# Revit family: Evoflat MSS_Circulation_RFA_1
name_source: partatom
category: Mechanical Equipment
units: mm (PartAtom-declared; Revit-internal decimal feet)

## family parameters
Always vertical = Yes
Classification = None
Cut with Voids When Loaded = No
OmniClass Number = 23.75.65.11.11
OmniClass Title = Heating Controllers
Part Type = Normal
Room Calculation Point = No
Round Connector Dimension = Use Diameter
Shared = No
Work Plane-Based = No

## types (9) — shared parameters
Circulation Pump = Yes
Connection = G 3/4 Internal Thread
D = 20 mm  [stored 0.0656168 ft]
Description = Flat Station
H1 = 5 mm  [stored 0.0164042 ft]
H2 = 13 mm
H3 = 575 mm  [stored 1.88648 ft]
H4 = 313 mm
Heating Capacity = 15 kW
Heating Circuit dT = 20 °C
Heating Flow Rate Supply = 645 l/h
Heating Total Pressure Loss Primary = 8 kPa
IfcExportAs = IfcFlowController
IfcExportType = EvoFlat MSS
Insulation Material = Danfoss EPP insulation
L = 545 mm  [stored 1.78806 ft]
L1 = 112 mm  [stored 0.367454 ft]
L1a = 43 mm  [stored 0.141076 ft]
LOD 200 = No
LOD 350 = Yes
Manufacturer = Danfoss
Max Supply Temperature = 95 °C
Nominal Pressure = PN 10
Nut size = 30 mm
Type Image = <None>
Voltage = 230 V
W = 150 mm
W1 = 44 mm  [stored 0.144357 ft]
Weight = 10.00 kg

## per-type parameters (varying)
| type | DHW Flow Rate Primary | DHW Pressure Loss Primary | DHW Tap Load 50°C | DHW Temperature DHS/DHR | DHW capacity | Front Insulation | HEX material | Model | Model Type | With Front Insulation |
| Evoflat MSS_Type 1_Cu_Circulation_145B1900 | 850 l/h | 40 kPa | 15.3 l/min | 65/22 °C | 43 kW | No | Danfoss Copper | 145B1900 | Evoflat MSS_Type 1_Cu_Circulation | No |
| Evoflat MSS_Type 2_Cu_Circulation_145B1903 | 950 l/h | 30 kPa | 17.5 l/min | 65/21 °C | 49 kW | No | Danfoss Copper | 145B1903 | Evoflat MSS_Type 2_Cu_Circulation | No |
| Evoflat MSS_Type 3_Cu_Circulation_145B1907 | 950 l/h | 27 kPa | 19.4 l/min | 65/16 °C | 55 kW | No | Danfoss Copper | 145B1907 | Evoflat MSS_Type 3_Cu_Circulation | No |
| Evoflat MSS_Type 1_Cu_Ins_Circulation_145B1910 | 850 l/h | 40 kPa | 15.3 l/min | 65/22 °C | 43 kW | Yes | Danfoss Copper | 145B1910 | Evoflat MSS_Type 1_Cu_Ins_Circulation | Yes |
| Evoflat MSS_Type 2_Cu_Ins_Circulation_145B1913 | 950 l/h | 30 kPa | 17.5 l/min | 65/21 °C | 49 kW | Yes | Danfoss Copper | 145B1913 | Evoflat MSS_Type 2_Cu_Ins_Circulation | Yes |
| Evoflat MSS_Type 3_Cu_Ins_Circulation_145B1917 | 950 l/h | 27 kPa | 19.4 l/min | 65/16 °C | 55 kW | Yes | Danfoss Copper | 145B1917 | Evoflat MSS_Type 3_Cu_Ins_Circulation | Yes |
| Evoflat MSS_Type 1_StS_Ins_Circulation_145B1954 | 850 l/h | 40 kPa | 15.3 l/min | 65/22 °C | 43 kW | Yes | Danfoss Stainless Steel | 145B1954 | Evoflat MSS_Type 1_StS_Ins_Circulation | Yes |
| Evoflat MSS_Type 2_StS_Ins_Circulation_145B1955 | 950 l/h | 30 kPa | 17.5 l/min | 65/21 °C | 49 kW | Yes | Danfoss Stainless Steel | 145B1955 | Evoflat MSS_Type 2_StS_Ins_Circulation | Yes |
| Evoflat MSS_Type 3_StS_Ins_Circulation_145B1956 | 950 l/h | 27 kPa | 19.4 l/min | 65/16 °C | 55 kW | Yes | Danfoss Stainless Steel | 145B1956 | Evoflat MSS_Type 3_StS_Ins_Circulation | Yes |

note: [stored X ft] marks values corroborated as IEEE doubles in the binary element streams (Revit-internal decimal feet)

## geometry (parser evidence)
native form markers: Sweep x10
no freeform markers — native parametric forms only
